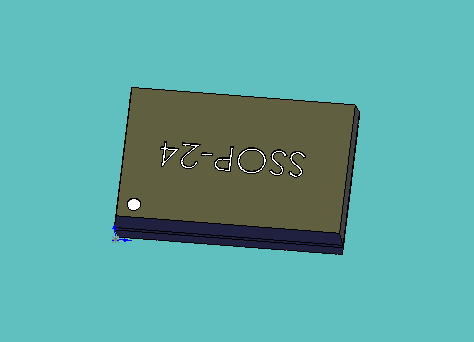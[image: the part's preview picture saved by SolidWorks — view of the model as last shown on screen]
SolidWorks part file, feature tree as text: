
SOLIDWORKS PART (.sldprt)
format: sldprt  version: not decoded by parser v0  size: 198,656 bytes
history: native  units: mm
features: sketch x3, chamfer x2, cut_extrude x2, material x1, extrude x1 (+15 scaffold rows collapsed)
feature tree (24):
  scaffold x15  (default folders/planes/origin — collapsed)
  material  "Material <not specified>"
  sketch  "Sketch1"
  extrude  "Extrude1"  Depth=1.8mm
  chamfer  "Chamfer1"  Distance=0.8mm Angle=7deg
  chamfer  "Chamfer2"  Distance=0.8mm Angle=7deg
  sketch  "Sketch3"  dims[D1=~0.283784mm]
  cut_extrude  "Cut-Extrude1"  Depth=0.05mm
  sketch  "Sketch4"
  cut_extrude  "Cut-Extrude2"  Depth=0.05mm
decode coverage: 6 of 8 modeling features carry decoded parameters
note: ~ marks probable driven/reference dimensions
note: suppression state not decoded; provenance and decode notes live in map.json
